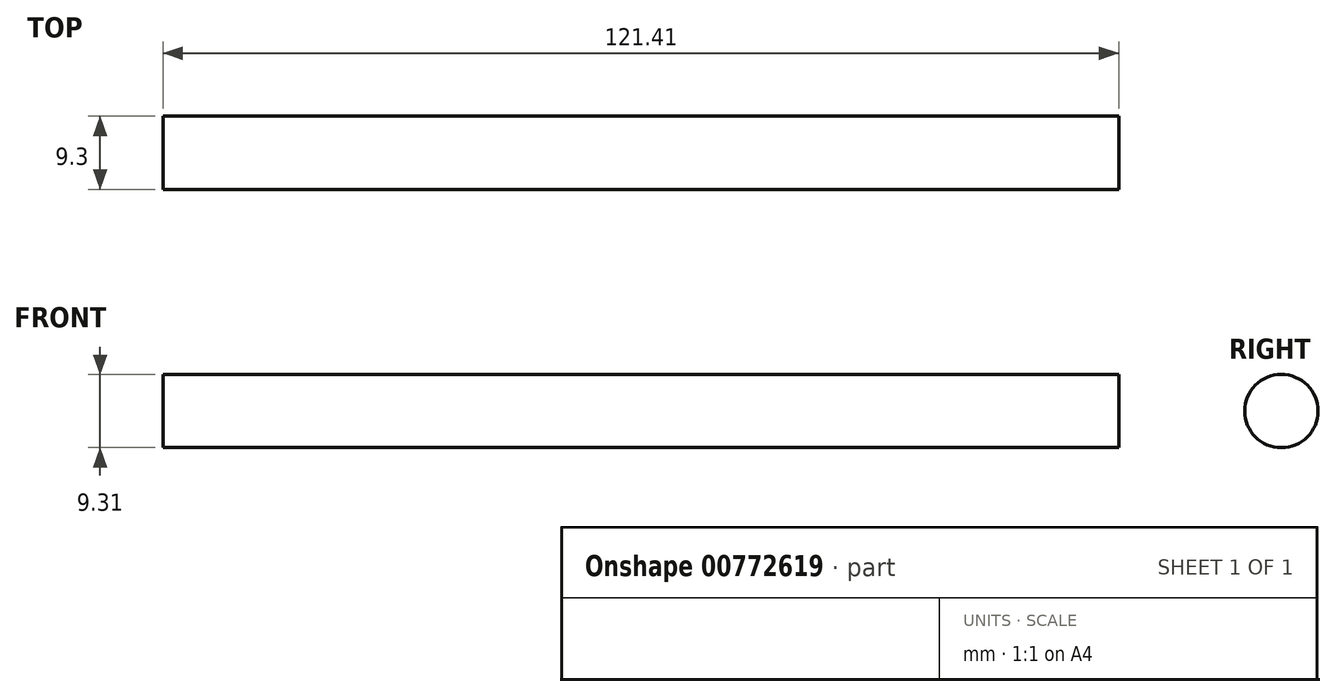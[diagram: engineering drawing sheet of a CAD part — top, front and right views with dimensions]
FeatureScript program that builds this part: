
annotation { "Feature Type Name" : "Feature", "Feature Type Description" : "" }
export const myFeature = defineFeature(function(context is Context, id is Id, definition is map)
    precondition{}
    {
        {
            var Q0;
            Q0=qCreatedBy(makeId("Front.planeOp"),FACE);
            var sketch = newSketch(context, id + "F0", { "sketchPlane" : qUnion([Q0])});
            skLineSegment(sketch, "E0.bottom", {"start": v(-62.81, 14.96) * mm, "end": v(58.6, 14.96) * mm});
            skLineSegment(sketch, "E0.top", {"start": v(-62.81, 10.3) * mm, "end": v(58.6, 10.3) * mm});
            skLineSegment(sketch, "E0.left", {"start": v(-62.81, 14.96) * mm, "end": v(-62.81, 10.3) * mm});
            skLineSegment(sketch, "E0.right", {"start": v(58.6, 14.96) * mm, "end": v(58.6, 10.3) * mm});
            skSolve(sketch);
        }
        {
            var Q0;
            Q0 = qSketchRegion(id + "F0", true);
            var Q1;
            Q1=sQuery(id+"F0.wireOp",EDGE,"E0.top");
            revolve(context, id + "F1", {"surfaceOperationType" : NewSurfaceOperationType.NEW, "entities" : qUnion([Q0]), "axis" : qUnion([Q1]), "revolveType" : RevolveType.FULL});
        }
    });
